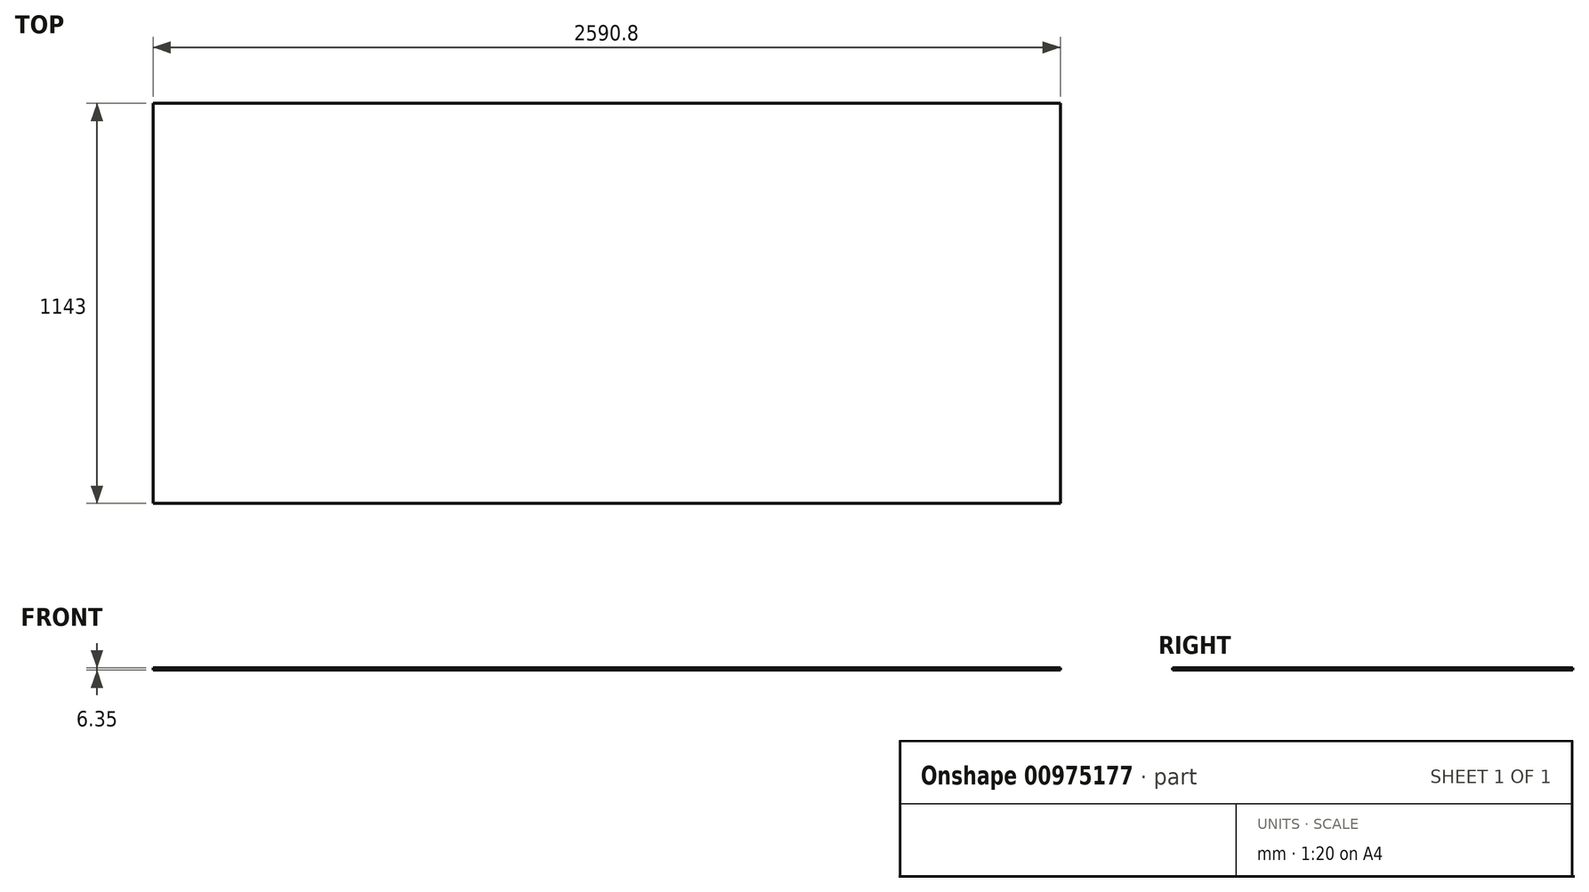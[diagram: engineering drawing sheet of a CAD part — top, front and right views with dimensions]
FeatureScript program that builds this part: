
annotation { "Feature Type Name" : "Feature", "Feature Type Description" : "" }
export const myFeature = defineFeature(function(context is Context, id is Id, definition is map)
    precondition{}
    {
        {
            var Q0;
            Q0=qCreatedBy(makeId("Top.planeOp"),FACE);
            var sketch = newSketch(context, id + "F0", { "sketchPlane" : qUnion([Q0])});
            skLineSegment(sketch, "E0.bottom", {"start": v(-2598.34, 1106.66) * mm, "end": v(-7.54, 1106.66) * mm});
            skLineSegment(sketch, "E0.top", {"start": v(-2598.34, -36.34) * mm, "end": v(-7.54, -36.34) * mm});
            skLineSegment(sketch, "E0.left", {"start": v(-2598.34, 1106.66) * mm, "end": v(-2598.34, -36.34) * mm});
            skLineSegment(sketch, "E0.right", {"start": v(-7.54, 1106.66) * mm, "end": v(-7.54, -36.34) * mm});
            skSolve(sketch);
        }
        {
            var Q0;
            Q0=makeQuery(id+"F0.imprint","IMPRINT",FACE,{"disambiguationData":[TD([[makeQuery(id+"F0.imprint","IMPRINT",EDGE,{"derivedFrom":sQuery(id+"F0.wireOp",EDGE,"E0.bottom")}),-1.0]])]});
            extrude(context, id + "F1", {"entities" : qUnion([Q0]), "depth" : 6.35 * mm, "offsetDistance" : 25.4 * mm});
        }
    });
